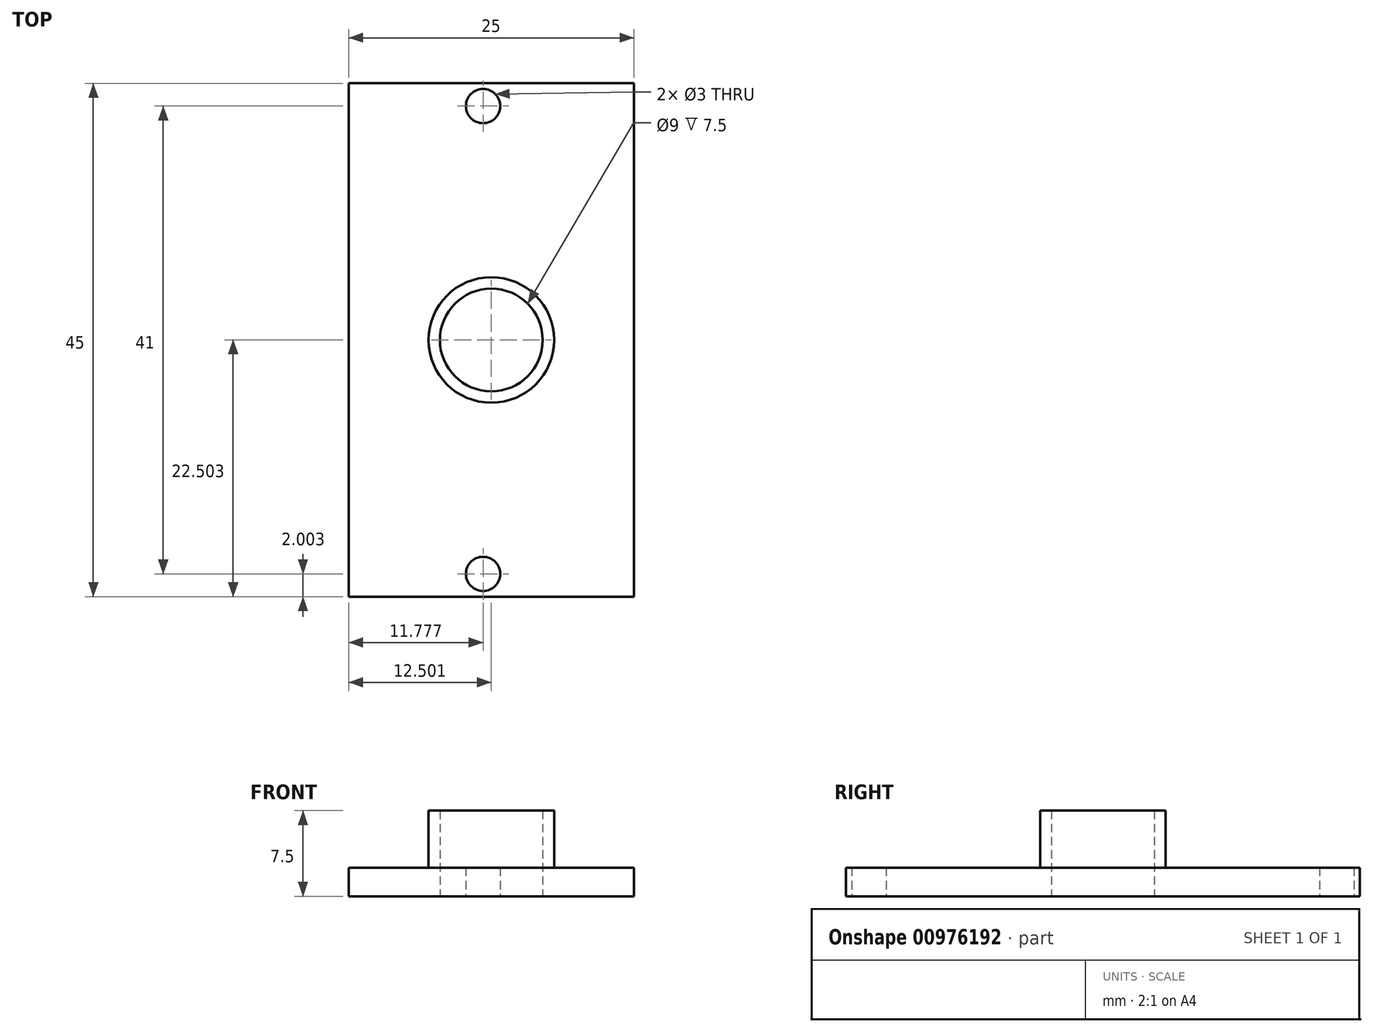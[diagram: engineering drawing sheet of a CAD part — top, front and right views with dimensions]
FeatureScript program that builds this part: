
annotation { "Feature Type Name" : "Feature", "Feature Type Description" : "" }
export const myFeature = defineFeature(function(context is Context, id is Id, definition is map)
    precondition{}
    {
        {
            var Q0;
            Q0=qCreatedBy(makeId("Top.planeOp"),FACE);
            var sketch = newSketch(context, id + "F0", { "sketchPlane" : qUnion([Q0])});
            skLineSegment(sketch, "E0.bottom", {"start": v(-24.52, 9.42) * mm, "end": v(0.48, 9.42) * mm});
            skLineSegment(sketch, "E0.top", {"start": v(-24.52, -35.58) * mm, "end": v(0.48, -35.58) * mm});
            skLineSegment(sketch, "E0.left", {"start": v(-24.52, 9.42) * mm, "end": v(-24.52, -35.58) * mm});
            skLineSegment(sketch, "E0.right", {"start": v(0.48, 9.42) * mm, "end": v(0.48, -35.58) * mm});
            skLineSegment(sketch, "E1", {"start": v(-24.52, -13.08) * mm, "end": v(0.48, -13.08) * mm, "construction": true});
            skCircle(sketch, "E2", {"center": v(-12.74, 7.42) * mm, "radius": 1.5 * mm});
            skCircle(sketch, "E3.MirrorC", {"center": v(-12.74, -33.58) * mm, "radius": 1.5 * mm});
            skCircle(sketch, "E4", {"center": v(-12.02, -13.08) * mm, "radius": 4.5 * mm});
            skCircle(sketch, "E5.0", {"center": v(-12.02, -13.08) * mm, "radius": 5.5 * mm});
            skSolve(sketch);
        }
        {
            var Q0;
            Q0=makeQuery(id+"F0.imprint","IMPRINT",FACE,{"disambiguationData":[TD([[makeQuery(id+"F0.imprint","IMPRINT",EDGE,{"derivedFrom":sQuery(id+"F0.wireOp",EDGE,"E0.bottom")}),-1.0]])]});
            var Q1;
            Q1=makeQuery(id+"F0.imprint","IMPRINT",FACE,{"disambiguationData":[TD([[makeQuery(id+"F0.imprint","IMPRINT",EDGE,{"derivedFrom":sQuery(id+"F0.wireOp",EDGE,"E4")}),-1.0]])]});
            extrude(context, id + "F1", {"entities" : qUnion([Q0, Q1]), "depth" : 2.5 * mm, "offsetDistance" : 25 * mm});
        }
        {
            var Q0;
            Q0=makeQuery(id+"F0.imprint","IMPRINT",FACE,{"disambiguationData":[TD([[makeQuery(id+"F0.imprint","IMPRINT",EDGE,{"derivedFrom":sQuery(id+"F0.wireOp",EDGE,"E4")}),-1.0]])]});
            extrude(context, id + "F2", {"entities" : qUnion([Q0]), "operationType" : NewBodyOperationType.ADD, "depth" : 7.5 * mm, "offsetDistance" : 25 * mm});
        }
    });
